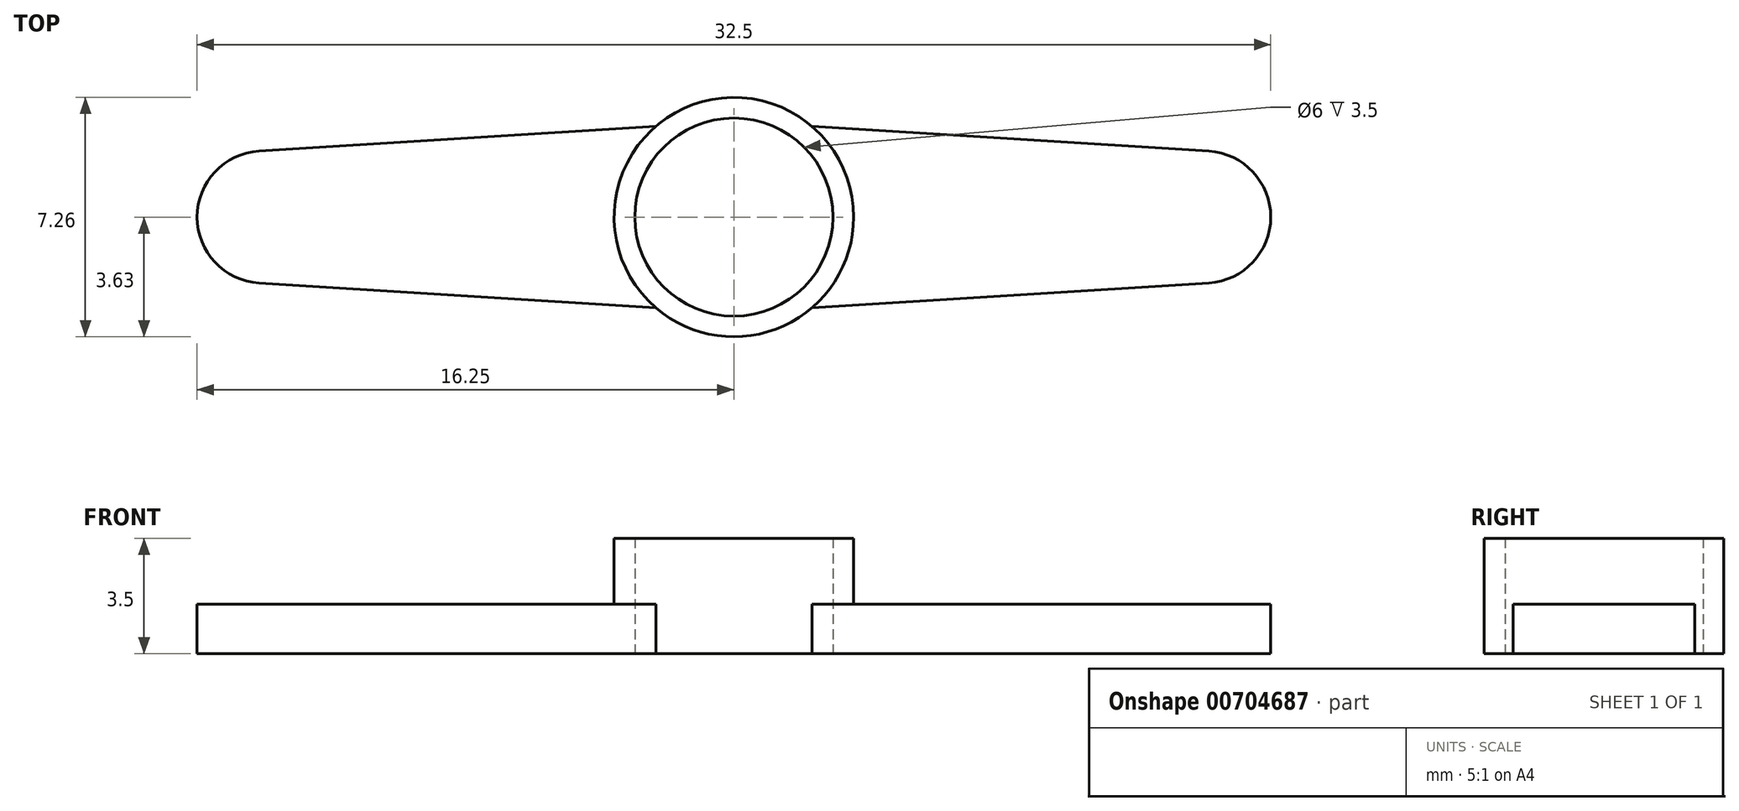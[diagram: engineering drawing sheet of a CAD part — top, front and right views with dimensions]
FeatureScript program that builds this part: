
annotation { "Feature Type Name" : "Feature", "Feature Type Description" : "" }
export const myFeature = defineFeature(function(context is Context, id is Id, definition is map)
    precondition{}
    {
        {
            var Q0;
            Q0=qCreatedBy(makeId("Top.planeOp"),FACE);
            var sketch = newSketch(context, id + "F0", { "sketchPlane" : qUnion([Q0])});
            skCircle(sketch, "E0", {"center": v(0, 0) * mm, "radius": 3.62 * mm});
            skCircle(sketch, "E1", {"center": v(14.25, 0) * mm, "radius": 2 * mm});
            skLineSegment(sketch, "E2", {"start": v(14.38, 2) * mm, "end": v(2.36, 2.75) * mm});
            skLineSegment(sketch, "E3", {"start": v(14.38, -2) * mm, "end": v(2.36, -2.75) * mm});
            skCircle(sketch, "E4", {"center": v(-14.25, 0) * mm, "radius": 2 * mm});
            skLineSegment(sketch, "E5", {"start": v(-14.38, 2) * mm, "end": v(-2.36, 2.75) * mm});
            skLineSegment(sketch, "E6", {"start": v(-14.38, -2) * mm, "end": v(-2.36, -2.75) * mm});
            skCircle(sketch, "E7", {"center": v(0, 0) * mm, "radius": 3 * mm});
            skSolve(sketch);
        }
        {
            var Q0;
            Q0=makeQuery(id+"F0.imprint","IMPRINT",FACE,{"disambiguationData":[TD([[makeQuery(id+"F0.imprint","IMPRINT",EDGE,{"derivedFrom":sQuery(id+"F0.wireOp",EDGE,"E7")}),-1.0]])]});
            extrude(context, id + "F1", {"entities" : qUnion([Q0]), "depth" : 3.5 * mm, "offsetDistance" : 25 * mm});
        }
        {
            var Q0;
            {var subQ0=sQuery(id+"F0.wireOp",EDGE,"E5");Q0=makeQuery(id+"F0.imprint","IMPRINT",FACE,{"disambiguationData":[TD([[makeQuery(id+"F0.imprint","IMPRINT",EDGE,{"derivedFrom":subQ0}),-1.0]])]});}
            var Q1;
            {var subQ0=sQuery(id+"F0.wireOp",EDGE,"E4");var subQ1=makeQuery(id+"F0.imprint","INTERSECT",VERTEX,{"derivedFrom":[subQ0,sQuery(id+"F0.wireOp",EDGE,"E5")]});Q1=makeQuery(id+"F0.imprint","IMPRINT",FACE,{"disambiguationData":[TD([[makeQuery(id+"F0.imprint","IMPRINT",EDGE,{"disambiguationData":[TD([[subQ1,-1.0]])],"derivedFrom":subQ0}),1.0]])]});}
            var Q2;
            {var subQ0=sQuery(id+"F0.wireOp",EDGE,"E2");Q2=makeQuery(id+"F0.imprint","IMPRINT",FACE,{"disambiguationData":[TD([[makeQuery(id+"F0.imprint","IMPRINT",EDGE,{"derivedFrom":subQ0}),1.0]])]});}
            var Q3;
            {var subQ0=sQuery(id+"F0.wireOp",EDGE,"E1");var subQ1=makeQuery(id+"F0.imprint","INTERSECT",VERTEX,{"derivedFrom":[subQ0,sQuery(id+"F0.wireOp",EDGE,"E2")]});Q3=makeQuery(id+"F0.imprint","IMPRINT",FACE,{"disambiguationData":[TD([[makeQuery(id+"F0.imprint","IMPRINT",EDGE,{"disambiguationData":[TD([[subQ1,-1.0]])],"derivedFrom":subQ0}),1.0]])]});}
            extrude(context, id + "F2", {"entities" : qUnion([Q0, Q1, Q2, Q3]), "operationType" : NewBodyOperationType.ADD, "depth" : 1.5 * mm, "offsetDistance" : 25 * mm});
        }
    });
